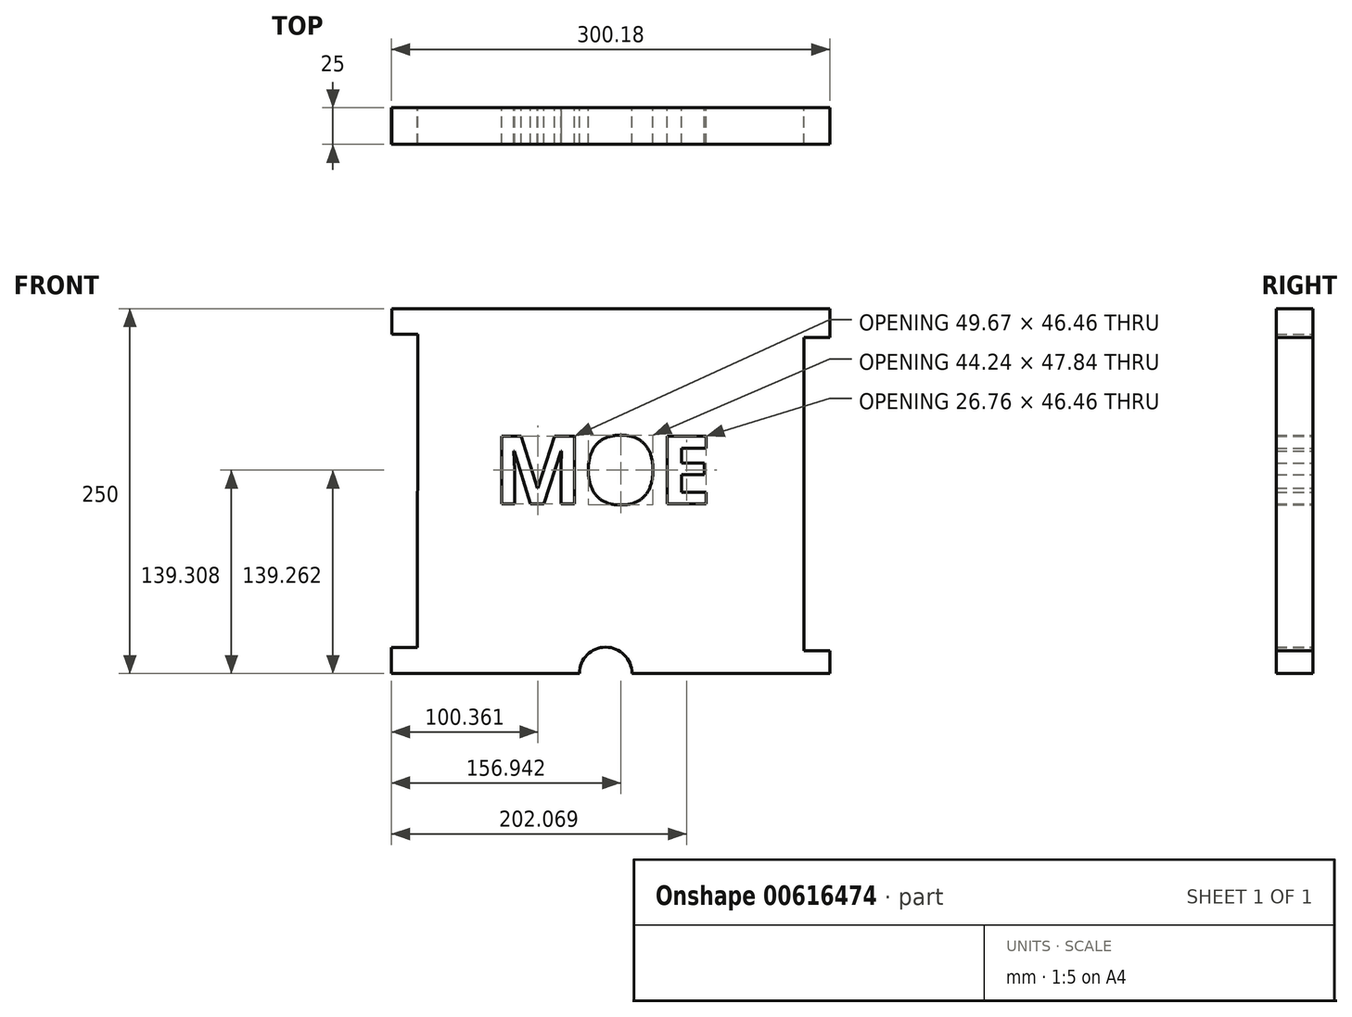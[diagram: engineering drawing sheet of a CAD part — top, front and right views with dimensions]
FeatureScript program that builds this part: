
annotation { "Feature Type Name" : "Feature", "Feature Type Description" : "" }
export const myFeature = defineFeature(function(context is Context, id is Id, definition is map)
    precondition{}
    {
        {
            var Q0;
            Q0=qCreatedBy(makeId("Front.planeOp"),FACE);
            var sketch = newSketch(context, id + "F0", { "sketchPlane" : qUnion([Q0])});
            skLineSegment(sketch, "E0.bottom", {"start": v(142.97, -77.06) * mm, "end": v(25.2, -77.06) * mm});
            skLineSegment(sketch, "E0.top", {"start": v(142.97, 172.94) * mm, "end": v(21.1, 172.94) * mm});
            skLineSegment(sketch, "E1.bottom", {"start": v(-121.81, -59.36) * mm, "end": v(-139.51, -59.36) * mm});
            skLineSegment(sketch, "E2.left", {"start": v(-121.42, 155.24) * mm, "end": v(-139.12, 155.24) * mm});
            skLineSegment(sketch, "E3.top", {"start": v(160.67, -61.4) * mm, "end": v(142.97, -61.4) * mm});
            skLineSegment(sketch, "E4.top", {"start": v(160.67, 153.2) * mm, "end": v(142.97, 153.2) * mm});
            skLineSegment(sketch, "E5", {"start": v(-139.12, 155.24) * mm, "end": v(-139.33, 155.24) * mm});
            skLineSegment(sketch, "E6", {"start": v(-121.42, 155.24) * mm, "end": v(-121.81, -59.36) * mm});
            skLineSegment(sketch, "E7", {"start": v(-139.12, 155.24) * mm, "end": v(-139.12, 172.94) * mm});
            skLineSegment(sketch, "E8", {"start": v(-139.51, -59.36) * mm, "end": v(-139.51, -77.06) * mm});
            skLineSegment(sketch, "E9", {"start": v(-139.12, 172.94) * mm, "end": v(-121.42, 172.94) * mm});
            skLineSegment(sketch, "E10", {"start": v(-139.51, -77.06) * mm, "end": v(-121.63, -77.06) * mm});
            skLineSegment(sketch, "E11", {"start": v(160.67, 153.2) * mm, "end": v(160.67, 172.94) * mm});
            skLineSegment(sketch, "E12", {"start": v(142.97, 172.94) * mm, "end": v(160.67, 172.94) * mm});
            skLineSegment(sketch, "E13", {"start": v(142.97, -77.06) * mm, "end": v(160.67, -77.06) * mm});
            skLineSegment(sketch, "E14", {"start": v(160.67, -61.4) * mm, "end": v(160.67, -77.06) * mm});
            skLineSegment(sketch, "E15", {"start": v(142.97, -61.4) * mm, "end": v(142.97, 153.2) * mm});
            skLineSegment(sketch, "E16.trimOffspring", {"start": v(-28.9, 172.94) * mm, "end": v(-121.42, 172.94) * mm});
            skLineSegment(sketch, "E17", {"start": v(21.1, 172.94) * mm, "end": v(-28.9, 172.94) * mm});
            skArc(sketch, "E18", {"start": v(25.2, -77.06) * mm, "mid": v(7.2, -59.06) * mm, "end": v(-10.8, -77.06) * mm});
            skLineSegment(sketch, "E19.trimOffspring", {"start": v(-10.8, -77.06) * mm, "end": v(-121.63, -77.06) * mm});
            skText(sketch, "E20", { "text": "MOE", "fontName": "OpenSans-Bold.ttf"});
            const initialGuessF0  = {"E20": [-0.06983, 0.03897, 1, 0, 0.04686]};
            skSetInitialGuess(sketch, initialGuessF0);
            skSolve(sketch);
        }
        {
            var Q0;
            Q0 = qSketchRegion(id + "F0", true);
            extrude(context, id + "F1", {"entities" : qUnion([Q0]), "depth" : 25 * mm, "offsetDistance" : 25 * mm});
        }
    });
